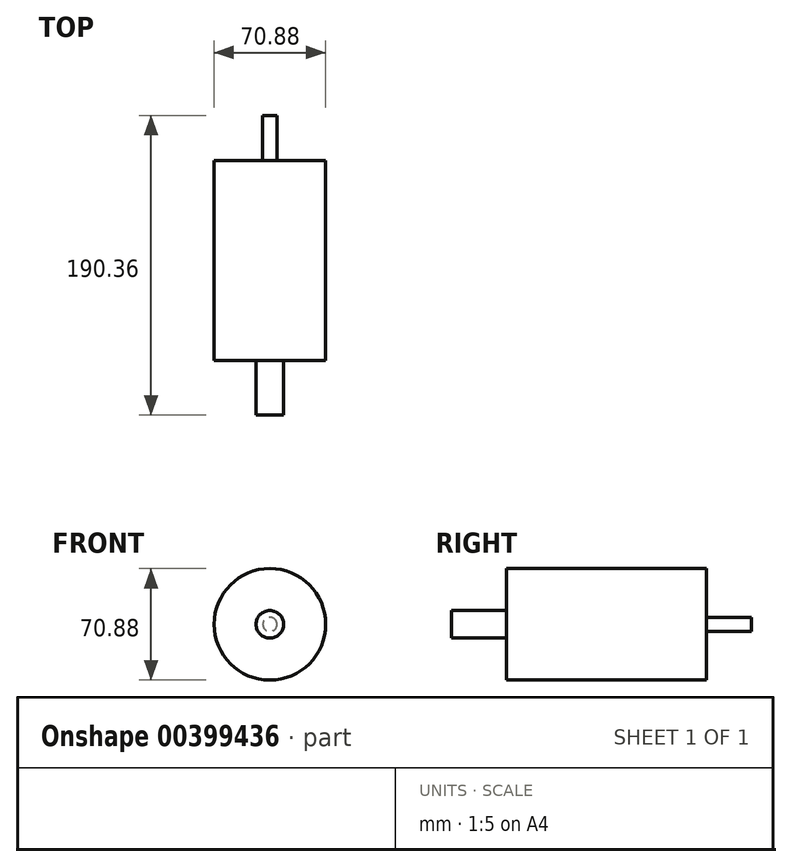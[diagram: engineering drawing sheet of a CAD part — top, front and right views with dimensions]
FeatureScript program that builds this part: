
annotation { "Feature Type Name" : "Feature", "Feature Type Description" : "" }
export const myFeature = defineFeature(function(context is Context, id is Id, definition is map)
    precondition{}
    {
        {
            var Q0;
            Q0=qCreatedBy(makeId("Front.planeOp"),FACE);
            var sketch = newSketch(context, id + "F0", { "sketchPlane" : qUnion([Q0])});
            skCircle(sketch, "E0", {"center": v(0, 0) * mm, "radius": 35.44 * mm});
            skSolve(sketch);
        }
        {
            var Q0;
            Q0=makeQuery(id+"F0.imprint","IMPRINT",FACE,{"disambiguationData":[TD([[makeQuery(id+"F0.imprint","IMPRINT",EDGE,{"derivedFrom":sQuery(id+"F0.wireOp",EDGE,"E0")}),1.0]])]});
            extrude(context, id + "F1", {"entities" : qUnion([Q0]), "depth" : 127 * mm});
        }
        {
            var Q0;
            Q0=qCreatedBy(makeId("Front.planeOp"),FACE);
            var sketch = newSketch(context, id + "F2", { "sketchPlane" : qUnion([Q0])});
            skCircle(sketch, "E1", {"center": v(0, 0) * mm, "radius": 8.74 * mm});
            skSolve(sketch);
        }
        {
            var Q0;
            Q0=makeQuery(id+"F2.imprint","IMPRINT",FACE,{"disambiguationData":[TD([[makeQuery(id+"F2.imprint","IMPRINT",EDGE,{"derivedFrom":sQuery(id+"F2.wireOp",EDGE,"E1")}),1.0]])]});
            var Q1;
            Q1=sQuery(id+"F2.wireOp",EDGE,"E1");
            extrude(context, id + "F3", {"entities" : qUnion([Q0]), "operationType" : NewBodyOperationType.ADD, "surfaceEntities" : qUnion([Q1]), "endBound" : BoundingType.THROUGH_ALL, "depth" : 25.4 * mm});
        }
        {
            var Q0;
            Q0=makeQuery(id+"F3.opExtrude","CAP_FACE",FACE,{"disambiguationData":[OSD([sQuery(id+"F2.wireOp",EDGE,"E1")])],"isStart":false});
            var sketch = newSketch(context, id + "F4", { "sketchPlane" : qUnion([Q0])});
            skCircle(sketch, "E2", {"center": v(0, 0) * mm, "radius": 4.52 * mm});
            skSolve(sketch);
        }
        {
            var Q0;
            Q0=makeQuery(id+"F4.imprint","IMPRINT",FACE,{"disambiguationData":[TD([[makeQuery(id+"F4.imprint","IMPRINT",EDGE,{"derivedFrom":sQuery(id+"F4.wireOp",EDGE,"E2")}),1.0]])]});
            extrude(context, id + "F5", {"entities" : qUnion([Q0]), "operationType" : NewBodyOperationType.ADD, "endBound" : BoundingType.THROUGH_ALL, "oppositeDirection" : true, "depth" : 25.4 * mm});
        }
    });
